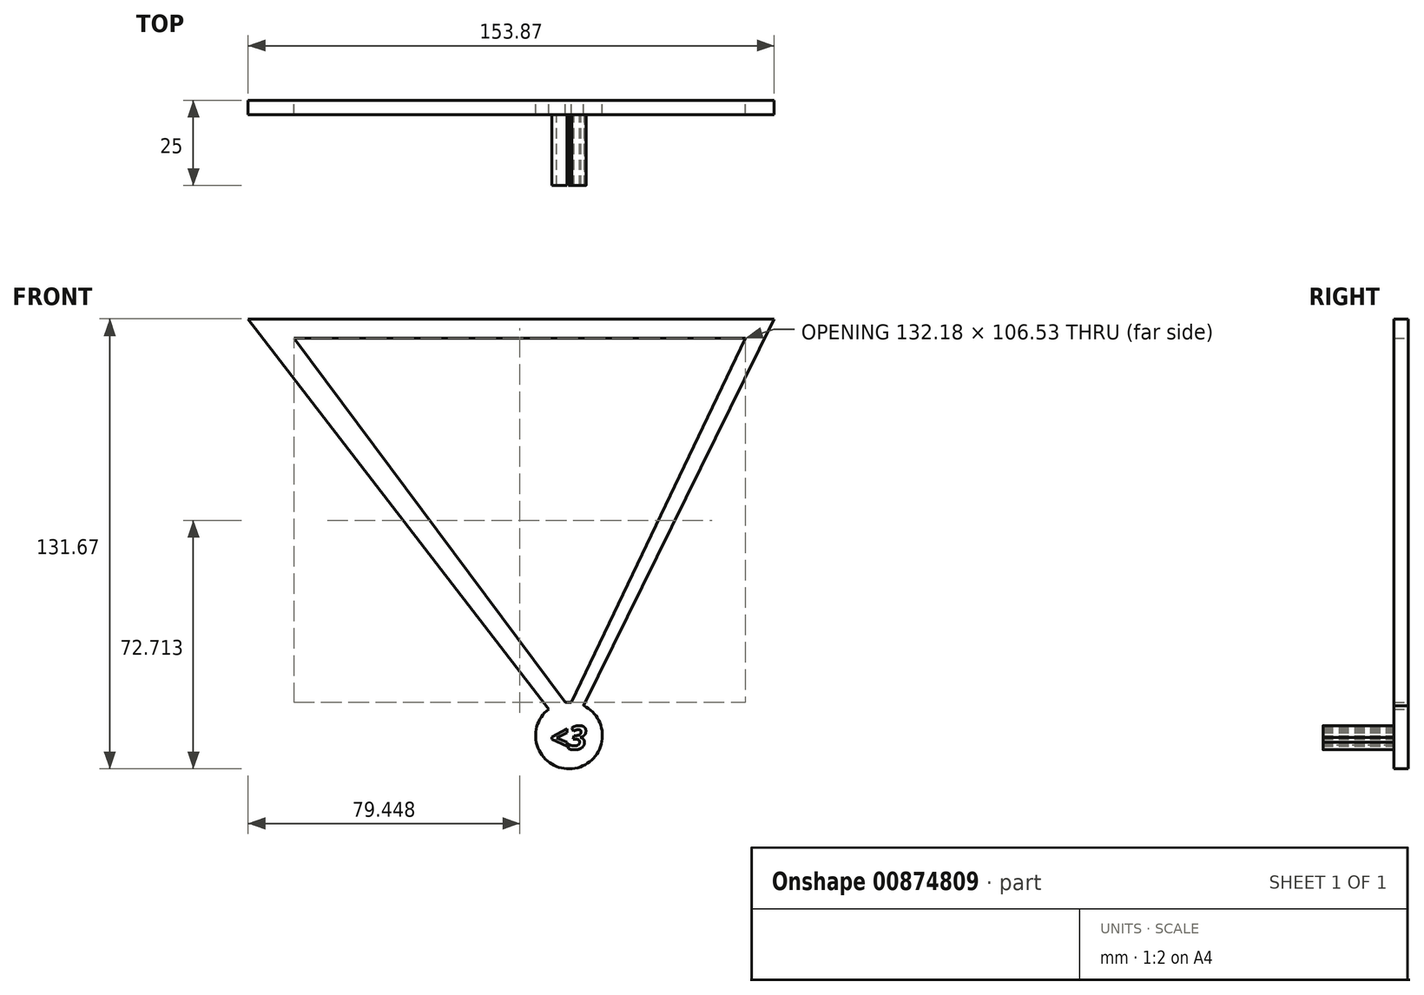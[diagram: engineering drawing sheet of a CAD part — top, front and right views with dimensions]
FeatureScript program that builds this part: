
annotation { "Feature Type Name" : "Feature", "Feature Type Description" : "" }
export const myFeature = defineFeature(function(context is Context, id is Id, definition is map)
    precondition{}
    {
        {
            var Q0;
            Q0=qCreatedBy(makeId("Front.planeOp"),FACE);
            var sketch = newSketch(context, id + "F0", { "sketchPlane" : qUnion([Q0])});
            skLineSegment(sketch, "E0", {"start": v(-93.88, 47.35) * mm, "end": v(59.99, 47.35) * mm});
            skLineSegment(sketch, "E1", {"start": v(-93.88, 47.35) * mm, "end": v(0, -74.56) * mm});
            skLineSegment(sketch, "E2", {"start": v(0, -74.56) * mm, "end": v(59.99, 47.35) * mm});
            skLineSegment(sketch, "E3", {"start": v(-80.52, 41.66) * mm, "end": v(51.66, 41.66) * mm});
            skLineSegment(sketch, "E4", {"start": v(51.66, 41.66) * mm, "end": v(0, -66.38) * mm});
            skLineSegment(sketch, "E5", {"start": v(0, -66.38) * mm, "end": v(-80.52, 41.66) * mm});
            skSolve(sketch);
        }
        {
            var Q0;
            Q0 = qSketchRegion(id + "F0", true);
            extrude(context, id + "F1", {"entities" : qUnion([Q0]), "depth" : 4.2 * mm, "offsetDistance" : 25 * mm});
        }
        {
            var Q0;
            Q0=qCreatedBy(makeId("Front.planeOp"),FACE);
            var sketch = newSketch(context, id + "F2", { "sketchPlane" : qUnion([Q0])});
            skCircle(sketch, "E6", {"center": v(0, -74.56) * mm, "radius": 9.76 * mm});
            skSolve(sketch);
        }
        {
            var Q0;
            Q0 = qSketchRegion(id + "F2", true);
            extrude(context, id + "F3", {"entities" : qUnion([Q0]), "operationType" : NewBodyOperationType.ADD, "depth" : 4.2 * mm, "offsetDistance" : 25 * mm});
        }
        {
            var Q0;
            Q0=qCreatedBy(makeId("Front.planeOp"),FACE);
            var sketch = newSketch(context, id + "F4", { "sketchPlane" : qUnion([Q0])});
            skText(sketch, "E7", { "text": "<3", "fontName": "OpenSans-BoldItalic.ttf"});
            const initialGuessF4  = {"E7": [-0.00558, -0.07866, 1, 0, 0.00696]};
            skSetInitialGuess(sketch, initialGuessF4);
            skSolve(sketch);
        }
        {
            var Q0;
            Q0 = qSketchRegion(id + "F4", true);
            extrude(context, id + "F5", {"entities" : qUnion([Q0]), "operationType" : NewBodyOperationType.ADD, "depth" : 25 * mm, "offsetDistance" : 25 * mm});
        }
    });
